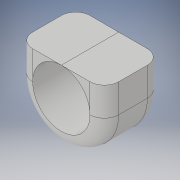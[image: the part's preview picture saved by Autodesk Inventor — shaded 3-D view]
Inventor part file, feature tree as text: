
AUTODESK INVENTOR PART (.ipt)
format: ipt  version: 2019 (Build 230136000, 136)  size: 136,704 bytes
history: native  units: mm
features: other x1, extrude x1, fillet x1, sketch x1
ambient origin geometry x8: Origin, YZ Plane, XZ Plane, XY Plane, X Axis, Y Axis, Z Axis, Center Point
bodies: Body1 (feature_tree)
feature tree (4):
  other  "Bryła1"
  extrude  "Wyciągnięcie proste1"  Depth=1.0mm
  fillet  "Zaokrąglenie1"  Radius=1.5mm
  sketch  "Szkic1"
